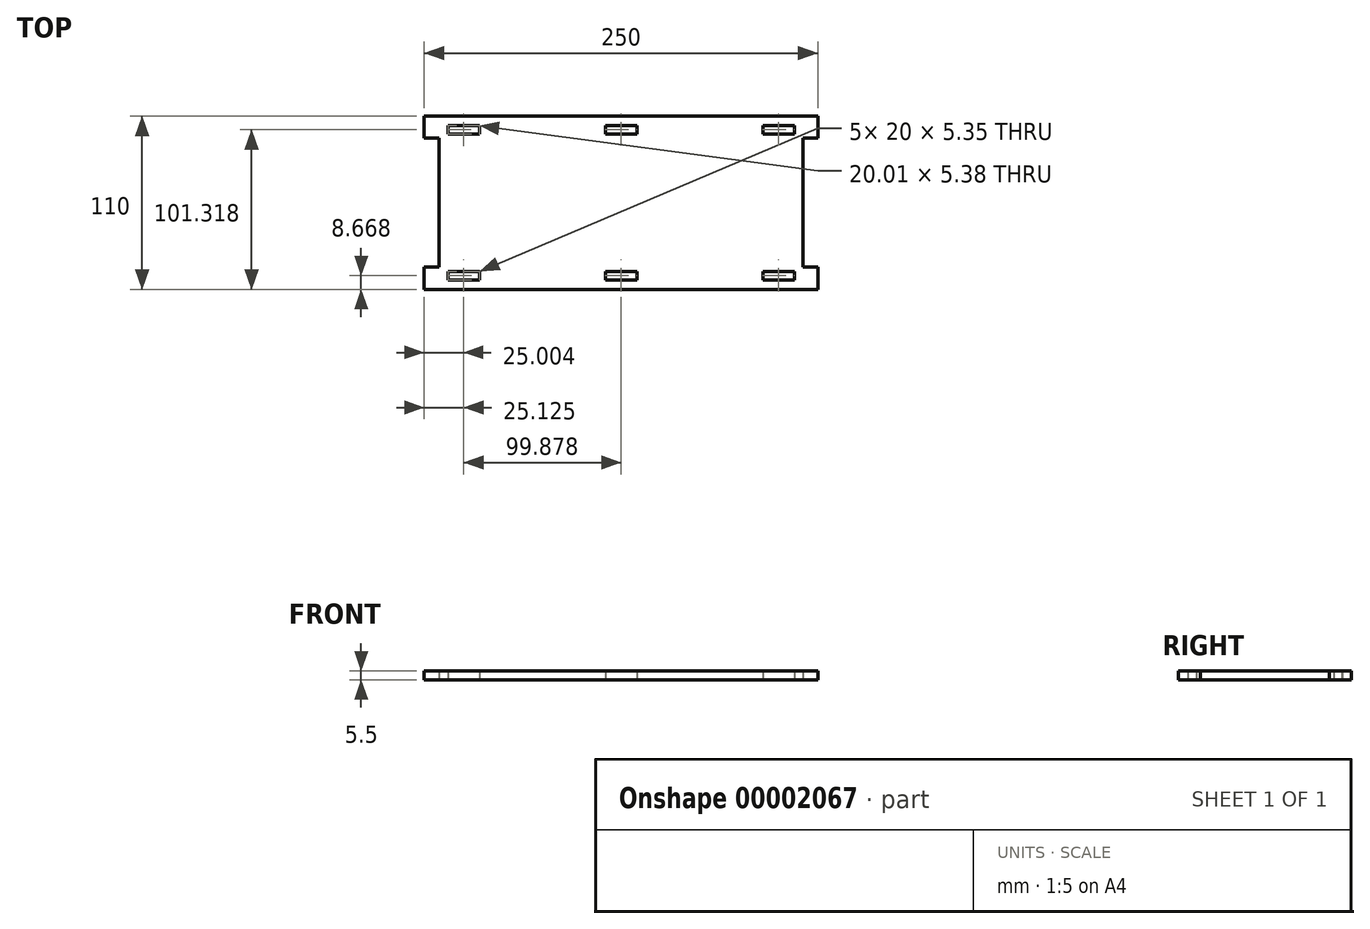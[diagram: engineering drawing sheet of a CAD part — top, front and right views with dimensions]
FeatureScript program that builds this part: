
annotation { "Feature Type Name" : "Feature", "Feature Type Description" : "" }
export const myFeature = defineFeature(function(context is Context, id is Id, definition is map)
    precondition{}
    {
        {
            var Q0;
            Q0=qCreatedBy(makeId("Top.planeOp"),FACE);
            var sketch = newSketch(context, id + "F0", { "sketchPlane" : qUnion([Q0])});
            skLineSegment(sketch, "E0.bottom", {"start": v(0, 0) * mm, "end": v(0, 0) * mm});
            skLineSegment(sketch, "E0.top", {"start": v(0, 53.66) * mm, "end": v(0, 53.66) * mm});
            skLineSegment(sketch, "E1.top", {"start": v(0, -56.34) * mm, "end": v(0, -56.34) * mm});
            skLineSegment(sketch, "E2.bottom", {"start": v(0, 53.66) * mm, "end": v(250, 53.66) * mm});
            skLineSegment(sketch, "E2.top", {"start": v(0, -56.34) * mm, "end": v(250, -56.34) * mm});
            skLineSegment(sketch, "E3", {"start": v(250, 44.52) * mm, "end": v(250, 39.66) * mm});
            skLineSegment(sketch, "E4", {"start": v(250, -47.2) * mm, "end": v(250, -56.34) * mm});
            skLineSegment(sketch, "E5", {"start": v(250, 44.52) * mm, "end": v(250, 53.66) * mm});
            skLineSegment(sketch, "E6", {"start": v(15, 42.29) * mm, "end": v(15, 47.64) * mm});
            skLineSegment(sketch, "E7", {"start": v(35, 42.32) * mm, "end": v(35, 47.67) * mm});
            skLineSegment(sketch, "E8", {"start": v(15.13, -45) * mm, "end": v(15.13, -50.35) * mm});
            skLineSegment(sketch, "E9", {"start": v(35.13, -45) * mm, "end": v(35.13, -50.35) * mm});
            skLineSegment(sketch, "E10", {"start": v(215, -50.35) * mm, "end": v(215, -45) * mm});
            skLineSegment(sketch, "E11", {"start": v(235, -50.35) * mm, "end": v(235, -45) * mm});
            skLineSegment(sketch, "E12", {"start": v(235, 42.32) * mm, "end": v(235, 47.67) * mm});
            skLineSegment(sketch, "E13", {"start": v(215, 42.32) * mm, "end": v(215, 47.67) * mm});
            skLineSegment(sketch, "E14", {"start": v(15, 47.64) * mm, "end": v(35, 47.67) * mm});
            skLineSegment(sketch, "E15", {"start": v(35, 42.32) * mm, "end": v(15, 42.29) * mm});
            skLineSegment(sketch, "E16", {"start": v(215, 42.32) * mm, "end": v(235, 42.32) * mm});
            skLineSegment(sketch, "E17", {"start": v(235, 47.67) * mm, "end": v(215, 47.67) * mm});
            skLineSegment(sketch, "E18", {"start": v(15.13, -45) * mm, "end": v(35.13, -45) * mm});
            skLineSegment(sketch, "E19", {"start": v(35.13, -50.35) * mm, "end": v(15.13, -50.35) * mm});
            skLineSegment(sketch, "E20", {"start": v(215, -50.35) * mm, "end": v(235, -50.35) * mm});
            skLineSegment(sketch, "E21", {"start": v(235, -45) * mm, "end": v(215, -45) * mm});
            skLineSegment(sketch, "E22", {"start": v(115, 42.32) * mm, "end": v(135, 42.32) * mm});
            skLineSegment(sketch, "E23", {"start": v(135, 42.32) * mm, "end": v(135, 47.67) * mm});
            skLineSegment(sketch, "E24", {"start": v(135, 47.67) * mm, "end": v(115, 47.67) * mm});
            skLineSegment(sketch, "E25", {"start": v(115, 47.67) * mm, "end": v(115, 42.32) * mm});
            skLineSegment(sketch, "E26", {"start": v(115, -45) * mm, "end": v(135, -45) * mm});
            skLineSegment(sketch, "E27", {"start": v(135, -45) * mm, "end": v(135, -50.35) * mm});
            skLineSegment(sketch, "E28", {"start": v(135, -50.35) * mm, "end": v(115, -50.35) * mm});
            skLineSegment(sketch, "E29", {"start": v(115, -50.35) * mm, "end": v(115, -45) * mm});
            skPoint(sketch, "E30", {"position": v(0, 39.66) * mm});
            skPoint(sketch, "E31", {"position": v(0, -42.34) * mm});
            skLineSegment(sketch, "E32", {"start": v(0, 39.66) * mm, "end": v(9.5, 39.66) * mm});
            skLineSegment(sketch, "E33", {"start": v(9.5, 39.66) * mm, "end": v(9.5, -42.34) * mm});
            skLineSegment(sketch, "E34", {"start": v(9.5, -42.34) * mm, "end": v(0, -42.34) * mm});
            skLineSegment(sketch, "E35.trimOffspring", {"start": v(0, -1.34) * mm, "end": v(0, 0) * mm});
            skPoint(sketch, "E36", {"position": v(250, -1.34) * mm});
            skPoint(sketch, "E37", {"position": v(250, 39.66) * mm});
            skPoint(sketch, "E38", {"position": v(250, -42.34) * mm});
            skLineSegment(sketch, "E39", {"start": v(250, 39.66) * mm, "end": v(240.5, 39.66) * mm});
            skLineSegment(sketch, "E40", {"start": v(240.5, 39.66) * mm, "end": v(240.5, -42.34) * mm});
            skLineSegment(sketch, "E41", {"start": v(240.5, -42.34) * mm, "end": v(250, -42.34) * mm});
            skLineSegment(sketch, "E42.trimOffspring", {"start": v(250, -42.34) * mm, "end": v(250, -47.2) * mm});
            skLineSegment(sketch, "E43", {"start": v(35.13, -45) * mm, "end": v(25.13, -45) * mm});
            skLineSegment(sketch, "E44", {"start": v(35, 42.32) * mm, "end": v(25, 42.3) * mm});
            skPoint(sketch, "E45.end.orphan", {"position": v(125, 53.66) * mm});
            skPoint(sketch, "E45.start.orphan", {"position": v(125, 47.67) * mm});
            skPoint(sketch, "E46.end.orphan", {"position": v(125, -50.35) * mm});
            skPoint(sketch, "E46.start.orphan", {"position": v(125, -56.34) * mm});
            skPoint(sketch, "E47.end.orphan", {"position": v(225, -45) * mm});
            skPoint(sketch, "E47.start.orphan", {"position": v(225, 42.32) * mm});
            skPoint(sketch, "E48.end.orphan", {"position": v(0, 44.52) * mm});
            skLineSegment(sketch, "E49", {"start": v(0, 53.66) * mm, "end": v(0, 39.66) * mm});
            skPoint(sketch, "E50.start.orphan", {"position": v(0, -47.2) * mm});
            skLineSegment(sketch, "E51", {"start": v(0, -42.34) * mm, "end": v(0, -56.34) * mm});
            skSolve(sketch);
        }
        {
            var Q0;
            Q0=makeQuery(id+"F0.imprint","IMPRINT",FACE,{"disambiguationData":[TD([[makeQuery(id+"F0.imprint","IMPRINT",EDGE,{"derivedFrom":sQuery(id+"F0.wireOp",EDGE,"E2.bottom")}),-1.0]])]});
            extrude(context, id + "F1", {"entities" : qUnion([Q0]), "depth" : 5.5 * mm});
        }
    });
